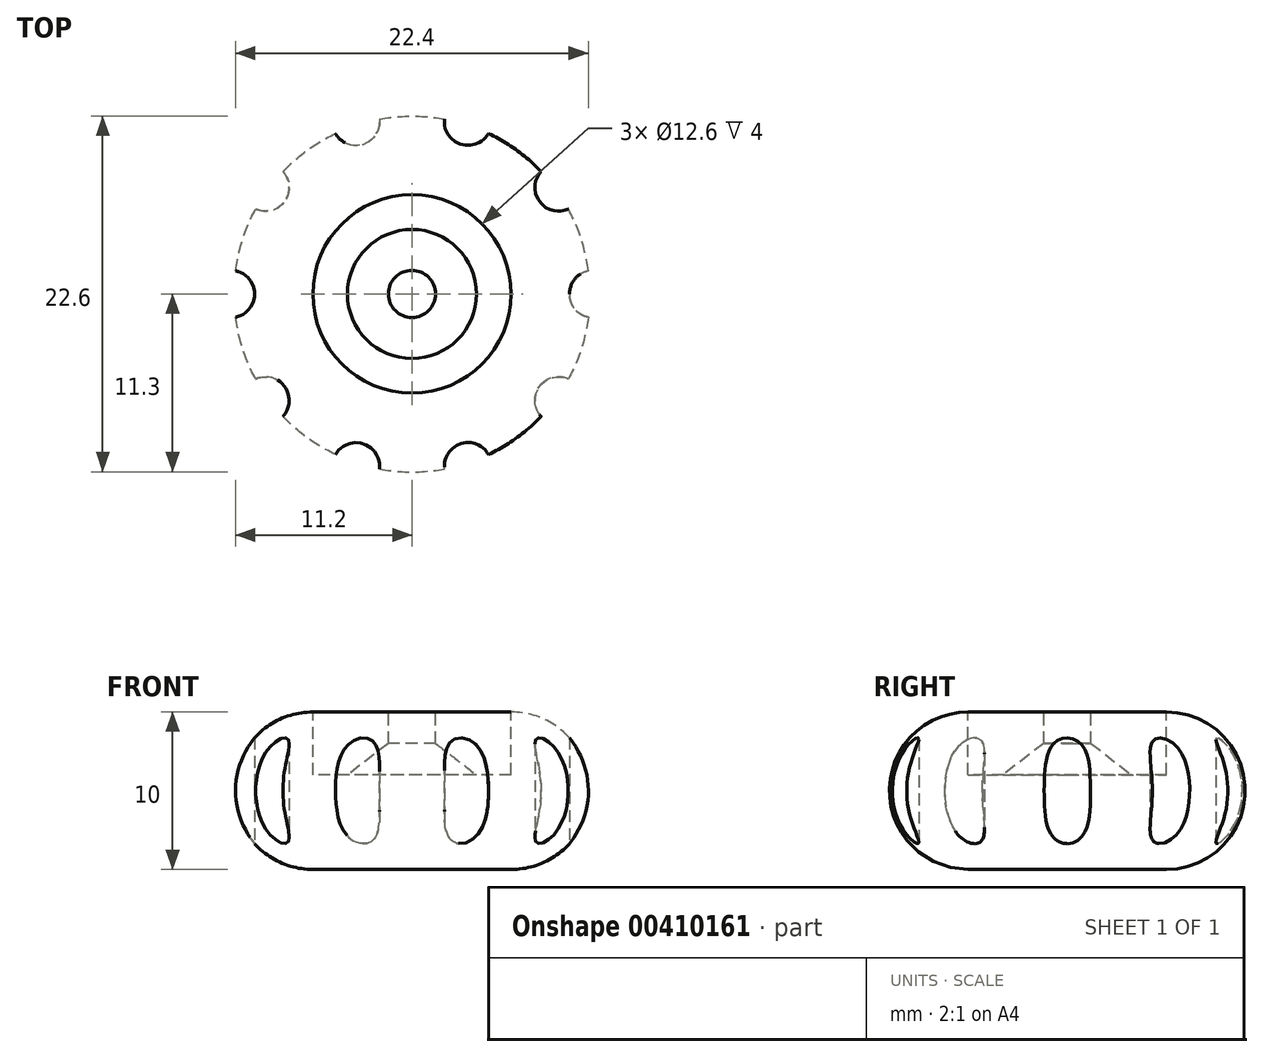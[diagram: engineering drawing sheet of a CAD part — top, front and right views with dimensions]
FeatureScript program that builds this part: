
annotation { "Feature Type Name" : "Feature", "Feature Type Description" : "" }
export const myFeature = defineFeature(function(context is Context, id is Id, definition is map)
    precondition{}
    {
        {
            var Q0;
            Q0=qCreatedBy(makeId("Front.planeOp"),FACE);
            var sketch = newSketch(context, id + "F0", { "sketchPlane" : qUnion([Q0])});
            skLineSegment(sketch, "E0", {"start": v(0, 0) * mm, "end": v(-6.3, 0) * mm});
            skLineSegment(sketch, "E1", {"start": v(-11.3, 5) * mm, "end": v(-11.3, 5) * mm});
            skLineSegment(sketch, "E2", {"start": v(-6.3, 10) * mm, "end": v(-6.3, 10) * mm});
            skLineSegment(sketch, "E3", {"start": v(-6.3, 10) * mm, "end": v(-6.3, 6) * mm});
            skLineSegment(sketch, "E4", {"start": v(0, 6) * mm, "end": v(0, 0) * mm});
            skPoint(sketch, "E5.visualSharp", {"position": v(-11.3, 10) * mm});
            skArc(sketch, "E5.filletArc", {"start": v(-6.3, 10) * mm, "mid": v(-9.84, 8.54) * mm, "end": v(-11.3, 5) * mm});
            skPoint(sketch, "E6.visualSharp", {"position": v(-11.3, 0) * mm});
            skArc(sketch, "E6.filletArc", {"start": v(-11.3, 5) * mm, "mid": v(-9.84, 1.46) * mm, "end": v(-6.3, 0) * mm});
            skLineSegment(sketch, "E7", {"start": v(-6.3, 6) * mm, "end": v(-4.1, 6) * mm});
            skLineSegment(sketch, "E8", {"start": v(-4.1, 6) * mm, "end": v(-1.5, 8) * mm});
            skLineSegment(sketch, "E9", {"start": v(-1.5, 8) * mm, "end": v(-1.5, 10) * mm});
            skLineSegment(sketch, "E10", {"start": v(-1.5, 10) * mm, "end": v(0, 10) * mm});
            skLineSegment(sketch, "E11", {"start": v(0, 10) * mm, "end": v(0, 6) * mm});
            skSolve(sketch);
        }
        {
            var Q0;
            Q0=makeQuery(id+"F0.imprint","IMPRINT",FACE,{"disambiguationData":[TD([[makeQuery(id+"F0.imprint","IMPRINT",EDGE,{"derivedFrom":sQuery(id+"F0.wireOp",EDGE,"E0")}),-1.0]])]});
            var Q1;
            Q1=sQuery(id+"F0.wireOp",EDGE,"E4");
            revolve(context, id + "F1", {"entities" : qUnion([Q0]), "axis" : qUnion([Q1]), "revolveType" : RevolveType.FULL});
        }
        {
            var Q0;
            Q0=makeQuery(id+"F1.opRevolve","SWEPT_FACE",FACE,{"disambiguationData":[OSD([sQuery(id+"F0.wireOp",EDGE,"E0")])]});
            var sketch = newSketch(context, id + "F2", { "sketchPlane" : qUnion([Q0])});
            skLineSegment(sketch, "E12", {"start": v(0, 0) * mm, "end": v(-16.48, 0) * mm, "construction": true});
            skCircle(sketch, "E13", {"center": v(-11.5, 0) * mm, "radius": 1.5 * mm});
            skCircle(sketch, "E14.1.0", {"center": v(-9.3, -6.76) * mm, "radius": 1.5 * mm});
            skCircle(sketch, "E14.2.0", {"center": v(-3.55, -10.94) * mm, "radius": 1.5 * mm});
            skCircle(sketch, "E14.3.0", {"center": v(3.55, -10.94) * mm, "radius": 1.5 * mm});
            skCircle(sketch, "E14.4.0", {"center": v(9.3, -6.76) * mm, "radius": 1.5 * mm});
            skCircle(sketch, "E14.5.0", {"center": v(11.5, 0) * mm, "radius": 1.5 * mm});
            skCircle(sketch, "E14.6.0", {"center": v(9.3, 6.76) * mm, "radius": 1.5 * mm});
            skCircle(sketch, "E14.7.0", {"center": v(3.55, 10.94) * mm, "radius": 1.5 * mm});
            skCircle(sketch, "E14.8.0", {"center": v(-3.55, 10.94) * mm, "radius": 1.5 * mm});
            skCircle(sketch, "E14.9.0", {"center": v(-9.3, 6.76) * mm, "radius": 1.5 * mm});
            skPoint(sketch, "E14.center", {"position": v(0, 0) * mm});
            skSolve(sketch);
        }
        {
            var Q0;
            Q0=makeQuery(id+"F2.imprint","IMPRINT",FACE,{"disambiguationData":[TD([[makeQuery(id+"F2.imprint","IMPRINT",EDGE,{"derivedFrom":sQuery(id+"F2.wireOp",EDGE,"E14.6.0")}),1.0]])]});
            var Q1;
            Q1=makeQuery(id+"F2.imprint","IMPRINT",FACE,{"disambiguationData":[TD([[makeQuery(id+"F2.imprint","IMPRINT",EDGE,{"derivedFrom":sQuery(id+"F2.wireOp",EDGE,"E14.5.0")}),1.0]])]});
            var Q2;
            Q2=makeQuery(id+"F2.imprint","IMPRINT",FACE,{"disambiguationData":[TD([[makeQuery(id+"F2.imprint","IMPRINT",EDGE,{"derivedFrom":sQuery(id+"F2.wireOp",EDGE,"E14.4.0")}),1.0]])]});
            var Q3;
            Q3=makeQuery(id+"F2.imprint","IMPRINT",FACE,{"disambiguationData":[TD([[makeQuery(id+"F2.imprint","IMPRINT",EDGE,{"derivedFrom":sQuery(id+"F2.wireOp",EDGE,"E14.3.0")}),1.0]])]});
            var Q4;
            Q4=makeQuery(id+"F2.imprint","IMPRINT",FACE,{"disambiguationData":[TD([[makeQuery(id+"F2.imprint","IMPRINT",EDGE,{"derivedFrom":sQuery(id+"F2.wireOp",EDGE,"E14.2.0")}),1.0]])]});
            var Q5;
            Q5=makeQuery(id+"F2.imprint","IMPRINT",FACE,{"disambiguationData":[TD([[makeQuery(id+"F2.imprint","IMPRINT",EDGE,{"derivedFrom":sQuery(id+"F2.wireOp",EDGE,"E14.1.0")}),1.0]])]});
            var Q6;
            Q6=makeQuery(id+"F2.imprint","IMPRINT",FACE,{"disambiguationData":[TD([[makeQuery(id+"F2.imprint","IMPRINT",EDGE,{"derivedFrom":sQuery(id+"F2.wireOp",EDGE,"E13")}),1.0]])]});
            var Q7;
            Q7=makeQuery(id+"F2.imprint","IMPRINT",FACE,{"disambiguationData":[TD([[makeQuery(id+"F2.imprint","IMPRINT",EDGE,{"derivedFrom":sQuery(id+"F2.wireOp",EDGE,"E14.9.0")}),1.0]])]});
            var Q8;
            Q8=makeQuery(id+"F2.imprint","IMPRINT",FACE,{"disambiguationData":[TD([[makeQuery(id+"F2.imprint","IMPRINT",EDGE,{"derivedFrom":sQuery(id+"F2.wireOp",EDGE,"E14.8.0")}),1.0]])]});
            var Q9;
            Q9=makeQuery(id+"F2.imprint","IMPRINT",FACE,{"disambiguationData":[TD([[makeQuery(id+"F2.imprint","IMPRINT",EDGE,{"derivedFrom":sQuery(id+"F2.wireOp",EDGE,"E14.7.0")}),1.0]])]});
            extrude(context, id + "F3", {"entities" : qUnion([Q0, Q1, Q2, Q3, Q4, Q5, Q6, Q7, Q8, Q9]), "operationType" : NewBodyOperationType.REMOVE, "oppositeDirection" : true, "depth" : 10 * mm});
        }
    });
